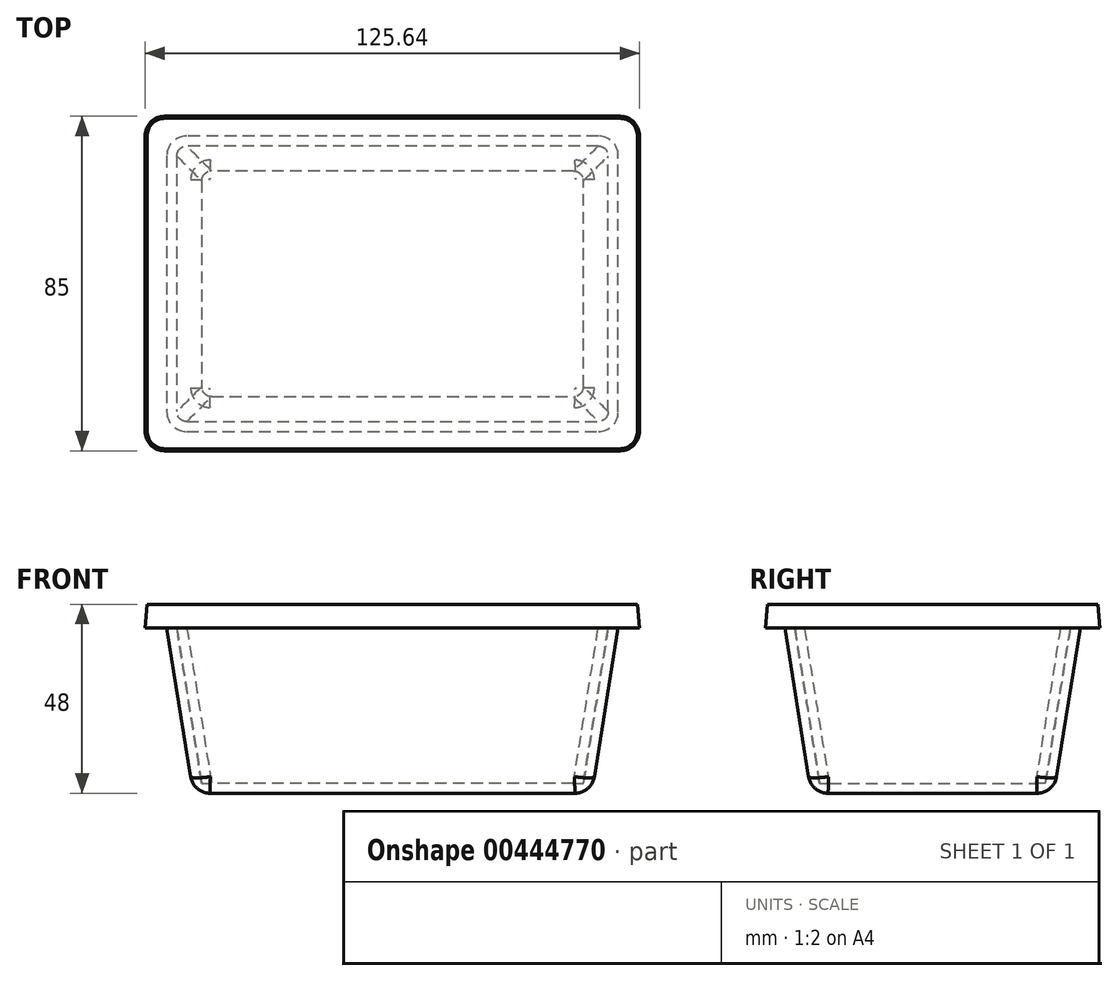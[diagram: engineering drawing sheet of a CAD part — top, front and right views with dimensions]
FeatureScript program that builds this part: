
annotation { "Feature Type Name" : "Feature", "Feature Type Description" : "" }
export const myFeature = defineFeature(function(context is Context, id is Id, definition is map)
    precondition{}
    {
        {
            var Q0;
            Q0=qCreatedBy(makeId("Top.planeOp"),FACE);
            var sketch = newSketch(context, id + "F0", { "sketchPlane" : qUnion([Q0])});
            skLineSegment(sketch, "E0", {"start": v(-73.85, 28.94) * mm, "end": v(-73.85, -22.69) * mm});
            skLineSegment(sketch, "E1", {"start": v(-68.85, -27.69) * mm, "end": v(22.37, -27.69) * mm});
            skLineSegment(sketch, "E2", {"start": v(27.37, -22.69) * mm, "end": v(27.37, 28.94) * mm});
            skLineSegment(sketch, "E3", {"start": v(22.37, 33.94) * mm, "end": v(-68.85, 33.94) * mm});
            skPoint(sketch, "E4.visualSharp", {"position": v(-73.85, 33.94) * mm});
            skArc(sketch, "E4.filletArc", {"start": v(-68.85, 33.94) * mm, "mid": v(-72.38, 32.48) * mm, "end": v(-73.85, 28.94) * mm});
            skPoint(sketch, "E5.visualSharp", {"position": v(27.37, 33.94) * mm});
            skArc(sketch, "E5.filletArc", {"start": v(27.37, 28.94) * mm, "mid": v(25.9, 32.48) * mm, "end": v(22.37, 33.94) * mm});
            skPoint(sketch, "E6.visualSharp", {"position": v(27.37, -27.69) * mm});
            skArc(sketch, "E6.filletArc", {"start": v(22.37, -27.69) * mm, "mid": v(25.9, -26.22) * mm, "end": v(27.37, -22.69) * mm});
            skPoint(sketch, "E7.visualSharp", {"position": v(-73.85, -27.69) * mm});
            skArc(sketch, "E7.filletArc", {"start": v(-73.85, -22.69) * mm, "mid": v(-72.38, -26.22) * mm, "end": v(-68.85, -27.69) * mm});
            skSolve(sketch);
        }
        {
            var Q0;
            Q0=qCreatedBy(makeId("Top.planeOp"),FACE);
            cPlane(context, id + "F1", {"entities" : qUnion([Q0]), "cplaneType" : CPlaneType.OFFSET, "offset" : 42 * mm, "width" : 150 * mm, "height" : 150 * mm});
        }
        {
            var Q0;
            Q0=qCreatedBy(id+"F1.planeOp",FACE);
            var sketch = newSketch(context, id + "F2", { "sketchPlane" : qUnion([Q0])});
            skLineSegment(sketch, "E8", {"start": v(-80.57, 35.66) * mm, "end": v(-80.57, -29.4) * mm});
            skLineSegment(sketch, "E9", {"start": v(-75.57, -34.4) * mm, "end": v(29.1, -34.4) * mm});
            skLineSegment(sketch, "E10", {"start": v(34.1, -29.4) * mm, "end": v(34.1, 35.66) * mm});
            skLineSegment(sketch, "E11", {"start": v(29.1, 40.66) * mm, "end": v(-75.57, 40.66) * mm});
            skPoint(sketch, "E12.visualSharp", {"position": v(-80.57, 40.66) * mm});
            skArc(sketch, "E12.filletArc", {"start": v(-75.57, 40.66) * mm, "mid": v(-79.1, 39.2) * mm, "end": v(-80.57, 35.66) * mm});
            skPoint(sketch, "E13.visualSharp", {"position": v(-80.57, -34.4) * mm});
            skArc(sketch, "E13.filletArc", {"start": v(-80.57, -29.4) * mm, "mid": v(-79.1, -32.94) * mm, "end": v(-75.57, -34.4) * mm});
            skPoint(sketch, "E14.visualSharp", {"position": v(34.1, -34.4) * mm});
            skArc(sketch, "E14.filletArc", {"start": v(29.1, -34.4) * mm, "mid": v(32.63, -32.94) * mm, "end": v(34.1, -29.4) * mm});
            skPoint(sketch, "E15.visualSharp", {"position": v(34.1, 40.66) * mm});
            skArc(sketch, "E15.filletArc", {"start": v(34.1, 35.66) * mm, "mid": v(32.63, 39.2) * mm, "end": v(29.1, 40.66) * mm});
            skSolve(sketch);
        }
        {
            var Q0;
            Q0=makeQuery(id+"F2.imprint","IMPRINT",FACE,{"disambiguationData":[TD([[makeQuery(id+"F2.imprint","IMPRINT",EDGE,{"derivedFrom":sQuery(id+"F2.wireOp",EDGE,"E8")}),1.0]])]});
            var Q1;
            Q1=makeQuery(id+"F0.imprint","IMPRINT",FACE,{"disambiguationData":[TD([[makeQuery(id+"F0.imprint","IMPRINT",EDGE,{"derivedFrom":sQuery(id+"F0.wireOp",EDGE,"E0")}),1.0]])]});
            loft(context, id + "F3", {"sheetProfilesArray" : [{ "sheetProfileEntities" : qUnion([Q0]) }, { "sheetProfileEntities" : qUnion([Q1]) }]});
        }
        {
            var Q0;
            Q0=makeQuery(id+"F3.opLoft","CAP_FACE",FACE,{"disambiguationData":[OSD([makeQuery(id+"F2.imprint","IMPRINT",FACE,{"disambiguationData":[TD([[makeQuery(id+"F2.imprint","IMPRINT",EDGE,{"derivedFrom":sQuery(id+"F2.wireOp",EDGE,"E8")}),1.0]])]})])],"isStart":true});
            shell(context, id + "F4", {"entities" : qUnion([Q0]), "thickness" : 2.5 * mm});
        }
        {
            var Q0;
            Q0=makeQuery(id+"F3.opLoft","CAP_FACE",FACE,{"disambiguationData":[OSD([makeQuery(id+"F2.imprint","IMPRINT",FACE,{"disambiguationData":[TD([[makeQuery(id+"F2.imprint","IMPRINT",EDGE,{"derivedFrom":sQuery(id+"F2.wireOp",EDGE,"E8")}),1.0]])]})])],"isStart":true});
            var sketch = newSketch(context, id + "F5", { "sketchPlane" : qUnion([Q0])});
            skLineSegment(sketch, "E16", {"start": v(-86.1, 40.7) * mm, "end": v(-86.1, -34.3) * mm});
            skLineSegment(sketch, "E17", {"start": v(-81.1, -39.3) * mm, "end": v(34.53, -39.3) * mm});
            skLineSegment(sketch, "E18", {"start": v(39.53, -34.3) * mm, "end": v(39.53, 40.7) * mm});
            skLineSegment(sketch, "E19", {"start": v(34.53, 45.7) * mm, "end": v(-81.1, 45.7) * mm});
            skPoint(sketch, "E20.visualSharp", {"position": v(-86.1, 45.7) * mm});
            skArc(sketch, "E20.filletArc", {"start": v(-81.1, 45.7) * mm, "mid": v(-84.64, 44.23) * mm, "end": v(-86.1, 40.7) * mm});
            skPoint(sketch, "E21.visualSharp", {"position": v(39.53, 45.7) * mm});
            skArc(sketch, "E21.filletArc", {"start": v(39.53, 40.7) * mm, "mid": v(38.07, 44.23) * mm, "end": v(34.53, 45.7) * mm});
            skPoint(sketch, "E22.visualSharp", {"position": v(39.53, -39.3) * mm});
            skArc(sketch, "E22.filletArc", {"start": v(34.53, -39.3) * mm, "mid": v(38.07, -37.84) * mm, "end": v(39.53, -34.3) * mm});
            skPoint(sketch, "E23.visualSharp", {"position": v(-86.1, -39.3) * mm});
            skArc(sketch, "E23.filletArc", {"start": v(-86.1, -34.3) * mm, "mid": v(-84.64, -37.84) * mm, "end": v(-81.1, -39.3) * mm});
            skSolve(sketch);
        }
        {
            var Q0;
            Q0 = qSketchRegion(id + "F5", true);
            extrude(context, id + "F6", {"entities" : qUnion([Q0]), "operationType" : NewBodyOperationType.ADD, "depth" : 6 * mm, "hasDraft" : true, "draftAngle" : 5 * degree, "draftPullDirection" : true});
        }
        {
            var Q0;
            Q0=makeQuery(id+"F3.opLoft","MID_CAP_EDGE",EDGE,{"disambiguationData":[OSD([sQuery(id+"F0.wireOp",EDGE,"E0"),sQuery(id+"F0.wireOp",EDGE,"E1"),sQuery(id+"F0.wireOp",EDGE,"E7.filletArc")])],"capPos":1.0});
            fillet(context, id + "F7", {"entities" : qUnion([Q0]), "radius" : 5 * mm, "tangentPropagation" : true, "allowEdgeOverflow" : false});
        }
    });
